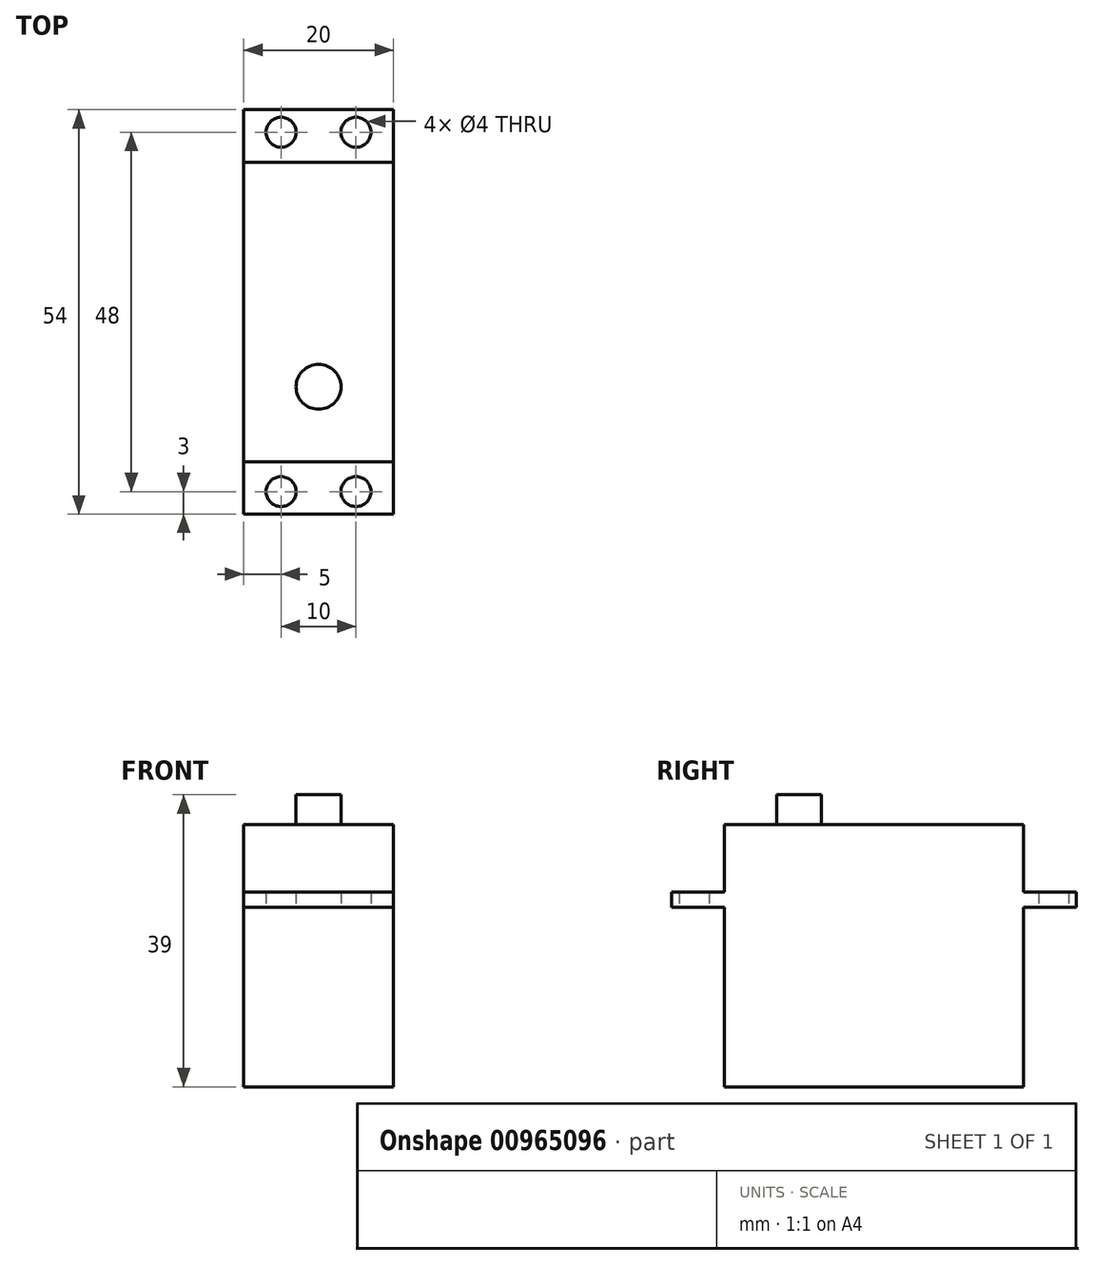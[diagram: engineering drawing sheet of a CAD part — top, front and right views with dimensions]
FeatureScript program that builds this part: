
annotation { "Feature Type Name" : "Feature", "Feature Type Description" : "" }
export const myFeature = defineFeature(function(context is Context, id is Id, definition is map)
    precondition{}
    {
        {
            var Q0;
            Q0=qCreatedBy(makeId("Top.planeOp"),FACE);
            var sketch = newSketch(context, id + "F0", { "sketchPlane" : qUnion([Q0])});
            skLineSegment(sketch, "E0.bottom", {"start": v(0, 0) * mm, "end": v(20, 0) * mm});
            skLineSegment(sketch, "E0.top", {"start": v(0, 54) * mm, "end": v(20, 54) * mm});
            skLineSegment(sketch, "E0.left", {"start": v(0, 0) * mm, "end": v(0, 54) * mm});
            skLineSegment(sketch, "E0.right", {"start": v(20, 0) * mm, "end": v(20, 54) * mm});
            skLineSegment(sketch, "E1", {"start": v(20, 47) * mm, "end": v(0, 47) * mm});
            skLineSegment(sketch, "E2", {"start": v(20, 7) * mm, "end": v(0, 7) * mm});
            skCircle(sketch, "E3", {"center": v(5, 51) * mm, "radius": 2 * mm});
            skCircle(sketch, "E4", {"center": v(15, 51) * mm, "radius": 2 * mm});
            skCircle(sketch, "E5", {"center": v(5, 3) * mm, "radius": 2 * mm});
            skCircle(sketch, "E6", {"center": v(15, 3) * mm, "radius": 2 * mm});
            skSolve(sketch);
        }
        {
            var Q0;
            {var subQ2=sQuery(id+"F0.wireOp",EDGE,"E0.top");Q0=makeQuery(id+"F0.imprint","IMPRINT",FACE,{"disambiguationData":[TD([[makeQuery(id+"F0.imprint","IMPRINT",EDGE,{"derivedFrom":subQ2}),-1.0]])]});}
            var Q1;
            {var subQ0=sQuery(id+"F0.wireOp",EDGE,"E1");Q1=makeQuery(id+"F0.imprint","IMPRINT",FACE,{"disambiguationData":[TD([[makeQuery(id+"F0.imprint","IMPRINT",EDGE,{"derivedFrom":subQ0}),1.0]])]});}
            var Q2;
            {var subQ2=sQuery(id+"F0.wireOp",EDGE,"E0.bottom");Q2=makeQuery(id+"F0.imprint","IMPRINT",FACE,{"disambiguationData":[TD([[makeQuery(id+"F0.imprint","IMPRINT",EDGE,{"derivedFrom":subQ2}),1.0]])]});}
            extrude(context, id + "F1", {"entities" : qUnion([Q0, Q1, Q2]), "depth" : 2 * mm, "offsetDistance" : 25 * mm});
        }
        {
            var Q0;
            {var subQ0=sQuery(id+"F0.wireOp",EDGE,"E1");Q0=makeQuery(id+"F0.imprint","IMPRINT",FACE,{"disambiguationData":[TD([[makeQuery(id+"F0.imprint","IMPRINT",EDGE,{"derivedFrom":subQ0}),1.0]])]});}
            extrude(context, id + "F2", {"entities" : qUnion([Q0]), "operationType" : NewBodyOperationType.ADD, "depth" : 11 * mm, "offsetDistance" : 25 * mm});
        }
        {
            var Q0;
            {var subQ0=sQuery(id+"F0.wireOp",EDGE,"E1");Q0=makeQuery(id+"F0.imprint","IMPRINT",FACE,{"disambiguationData":[TD([[makeQuery(id+"F0.imprint","IMPRINT",EDGE,{"derivedFrom":subQ0}),1.0]])]});}
            extrude(context, id + "F3", {"entities" : qUnion([Q0]), "operationType" : NewBodyOperationType.ADD, "oppositeDirection" : true, "depth" : 24 * mm, "offsetDistance" : 25 * mm});
        }
        {
            var Q0;
            Q0=makeQuery(id+"F2.opExtrude","CAP_FACE",FACE,{"disambiguationData":[OSD([sQuery(id+"F0.wireOp",EDGE,"E0.left"),sQuery(id+"F0.wireOp",EDGE,"E0.right"),sQuery(id+"F0.wireOp",EDGE,"E1"),sQuery(id+"F0.wireOp",EDGE,"E2")])],"isStart":false});
            var sketch = newSketch(context, id + "F4", { "sketchPlane" : qUnion([Q0])});
            skCircle(sketch, "E7", {"center": v(10, 17) * mm, "radius": 3 * mm});
            skSolve(sketch);
        }
        {
            var Q0;
            Q0=makeQuery(id+"F4.imprint","IMPRINT",FACE,{"disambiguationData":[TD([[makeQuery(id+"F4.imprint","IMPRINT",EDGE,{"derivedFrom":sQuery(id+"F4.wireOp",EDGE,"E7")}),1.0]])]});
            extrude(context, id + "F5", {"entities" : qUnion([Q0]), "operationType" : NewBodyOperationType.ADD, "depth" : 4 * mm, "offsetDistance" : 25 * mm});
        }
    });
